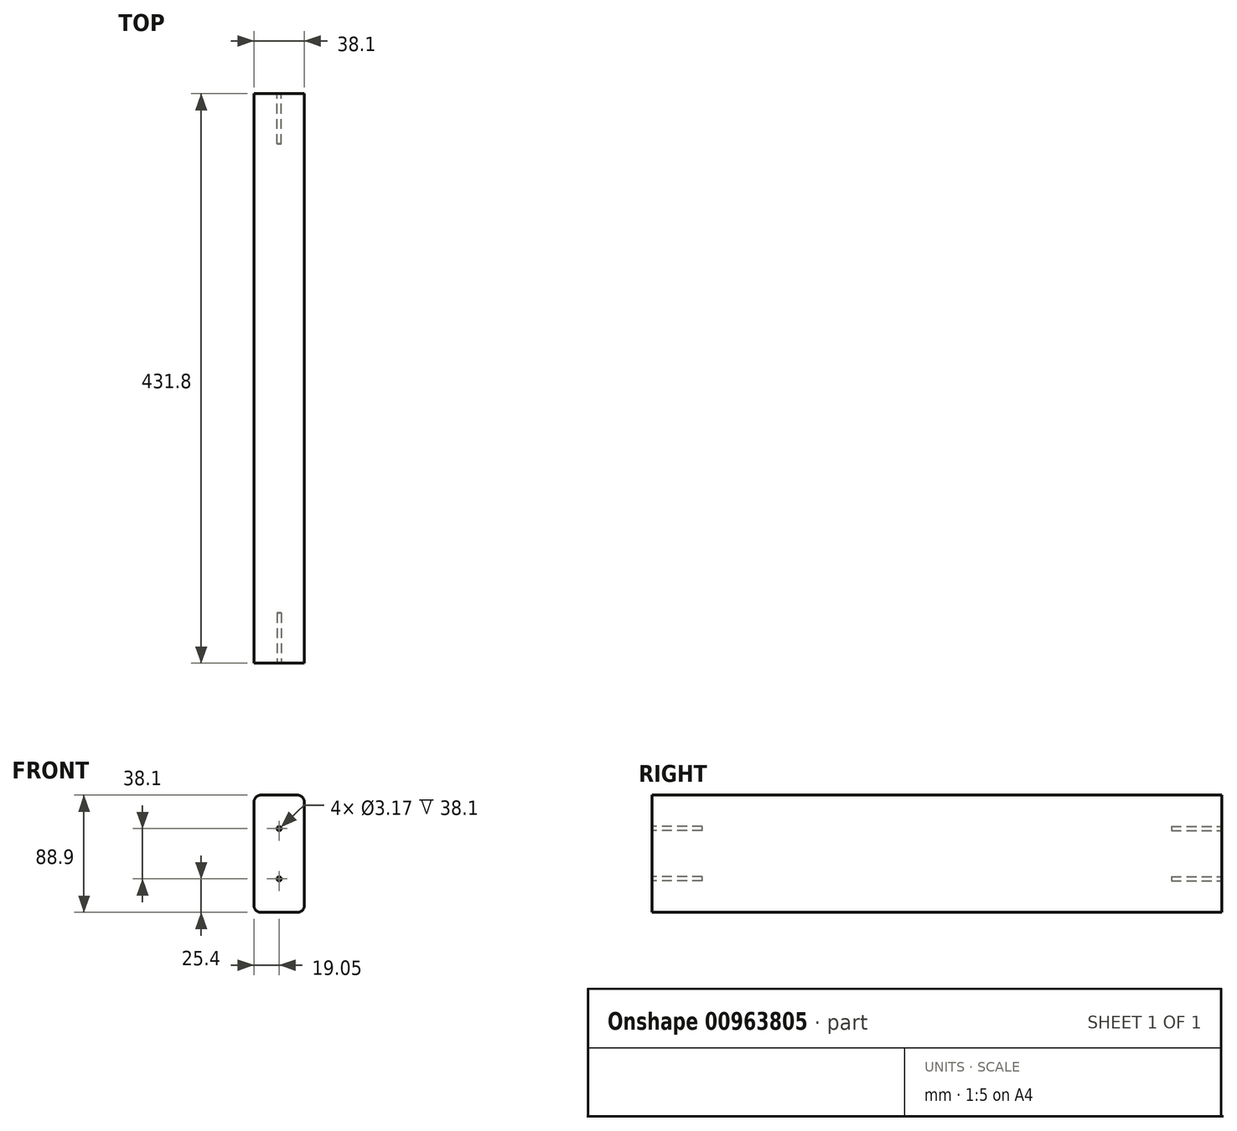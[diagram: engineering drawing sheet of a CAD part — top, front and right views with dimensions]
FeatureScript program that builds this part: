
annotation { "Feature Type Name" : "Feature", "Feature Type Description" : "" }
export const myFeature = defineFeature(function(context is Context, id is Id, definition is map)
    precondition{}
    {
        {
            var Q0;
            Q0=qCreatedBy(makeId("Front.planeOp"),FACE);
            var sketch = newSketch(context, id + "F0", { "sketchPlane" : qUnion([Q0])});
            skLineSegment(sketch, "E0.bottom", {"start": v(19.05, 44.45) * mm, "end": v(-19.05, 44.45) * mm});
            skLineSegment(sketch, "E0.top", {"start": v(19.05, -44.45) * mm, "end": v(-19.05, -44.45) * mm});
            skLineSegment(sketch, "E0.left", {"start": v(19.05, 44.45) * mm, "end": v(19.05, -44.45) * mm});
            skLineSegment(sketch, "E0.right", {"start": v(-19.05, 44.45) * mm, "end": v(-19.05, -44.45) * mm});
            skPoint(sketch, "E0.middle", {"position": v(0, 0) * mm});
            skSolve(sketch);
        }
        {
            var Q0;
            Q0=makeQuery(id+"F0.imprint","IMPRINT",FACE,{"disambiguationData":[TD([[makeQuery(id+"F0.imprint","IMPRINT",EDGE,{"derivedFrom":sQuery(id+"F0.wireOp",EDGE,"E0.bottom")}),1.0]])]});
            extrude(context, id + "F1", {"entities" : qUnion([Q0]), "endBound" : BoundingType.SYMMETRIC, "depth" : 431.8 * mm, "offsetDistance" : 25.4 * mm});
        }
        {
            var Q0;
            Q0=makeQuery(id+"F1.opExtrude","SWEPT_EDGE",EDGE,{"disambiguationData":[OSD([sQuery(id+"F0.wireOp",EDGE,"E0.bottom"),sQuery(id+"F0.wireOp",EDGE,"E0.left")])]});
            var Q1;
            Q1=makeQuery(id+"F1.opExtrude","SWEPT_EDGE",EDGE,{"disambiguationData":[OSD([sQuery(id+"F0.wireOp",EDGE,"E0.bottom"),sQuery(id+"F0.wireOp",EDGE,"E0.right")])]});
            var Q2;
            Q2=makeQuery(id+"F1.opExtrude","SWEPT_EDGE",EDGE,{"disambiguationData":[OSD([sQuery(id+"F0.wireOp",EDGE,"E0.top"),sQuery(id+"F0.wireOp",EDGE,"E0.left")])]});
            var Q3;
            Q3=makeQuery(id+"F1.opExtrude","SWEPT_EDGE",EDGE,{"disambiguationData":[OSD([sQuery(id+"F0.wireOp",EDGE,"E0.top"),sQuery(id+"F0.wireOp",EDGE,"E0.right")])]});
            fillet(context, id + "F2", {"entities" : qUnion([Q0, Q1, Q2, Q3]), "radius" : 5.08 * mm, "tangentPropagation" : true, "allowEdgeOverflow" : false});
        }
        {
            assignVariable(context, id + "F3", {"name" : "vbeam_h_drill_depth", "anyValue" : 38.1 * mm});
        }
        {
            var Q0;
            Q0=makeQuery(id+"F1.opExtrude","CAP_FACE",FACE,{"disambiguationData":[OSD([sQuery(id+"F0.wireOp",EDGE,"E0.bottom"),sQuery(id+"F0.wireOp",EDGE,"E0.top"),sQuery(id+"F0.wireOp",EDGE,"E0.left"),sQuery(id+"F0.wireOp",EDGE,"E0.right")])],"isStart":false});
            var sketch = newSketch(context, id + "F4", { "sketchPlane" : qUnion([Q0])});
            skCircle(sketch, "E1", {"center": v(0, 19.05) * mm, "radius": 1.59 * mm});
            skSolve(sketch);
        }
        {
            var Q0;
            Q0=makeQuery(id+"F4.imprint","IMPRINT",FACE,{"disambiguationData":[TD([[makeQuery(id+"F4.imprint","IMPRINT",EDGE,{"derivedFrom":sQuery(id+"F4.wireOp",EDGE,"E1")}),1.0]])]});
            extrude(context, id + "F5", {"entities" : qUnion([Q0]), "operationType" : NewBodyOperationType.REMOVE, "oppositeDirection" : true, "depth" : getVariable(context, 'vbeam_h_drill_depth'), "offsetDistance" : 25.4 * mm});
        }
        {
            var Q0;
            Q0=makeQuery(id+"F1.opExtrude","CAP_FACE",FACE,{"disambiguationData":[OSD([sQuery(id+"F0.wireOp",EDGE,"E0.bottom"),sQuery(id+"F0.wireOp",EDGE,"E0.top"),sQuery(id+"F0.wireOp",EDGE,"E0.left"),sQuery(id+"F0.wireOp",EDGE,"E0.right")])],"isStart":false});
            var sketch = newSketch(context, id + "F6", { "sketchPlane" : qUnion([Q0])});
            skCircle(sketch, "E2", {"center": v(0, -19.05) * mm, "radius": 1.59 * mm});
            skSolve(sketch);
        }
        {
            var Q0;
            Q0=makeQuery(id+"F6.imprint","IMPRINT",FACE,{"disambiguationData":[TD([[makeQuery(id+"F6.imprint","IMPRINT",EDGE,{"derivedFrom":sQuery(id+"F6.wireOp",EDGE,"E2")}),1.0]])]});
            extrude(context, id + "F7", {"entities" : qUnion([Q0]), "operationType" : NewBodyOperationType.REMOVE, "oppositeDirection" : true, "depth" : getVariable(context, 'vbeam_h_drill_depth'), "offsetDistance" : 25.4 * mm});
        }
        {
            var Q0;
            Q0=makeQuery(id+"F1.opExtrude","CAP_FACE",FACE,{"disambiguationData":[OSD([sQuery(id+"F0.wireOp",EDGE,"E0.bottom"),sQuery(id+"F0.wireOp",EDGE,"E0.top"),sQuery(id+"F0.wireOp",EDGE,"E0.left"),sQuery(id+"F0.wireOp",EDGE,"E0.right")])],"isStart":true});
            var sketch = newSketch(context, id + "F8", { "sketchPlane" : qUnion([Q0])});
            skCircle(sketch, "E3", {"center": v(0, 19.05) * mm, "radius": 1.59 * mm});
            skSolve(sketch);
        }
        {
            var Q0;
            Q0=makeQuery(id+"F8.imprint","IMPRINT",FACE,{"disambiguationData":[TD([[makeQuery(id+"F8.imprint","IMPRINT",EDGE,{"derivedFrom":sQuery(id+"F8.wireOp",EDGE,"E3")}),1.0]])]});
            extrude(context, id + "F9", {"entities" : qUnion([Q0]), "operationType" : NewBodyOperationType.REMOVE, "oppositeDirection" : true, "depth" : getVariable(context, 'vbeam_h_drill_depth'), "offsetDistance" : 25.4 * mm});
        }
        {
            var Q0;
            Q0=makeQuery(id+"F1.opExtrude","CAP_FACE",FACE,{"disambiguationData":[OSD([sQuery(id+"F0.wireOp",EDGE,"E0.bottom"),sQuery(id+"F0.wireOp",EDGE,"E0.top"),sQuery(id+"F0.wireOp",EDGE,"E0.left"),sQuery(id+"F0.wireOp",EDGE,"E0.right")])],"isStart":true});
            var sketch = newSketch(context, id + "F10", { "sketchPlane" : qUnion([Q0])});
            skCircle(sketch, "E4", {"center": v(0, -19.05) * mm, "radius": 1.59 * mm});
            skSolve(sketch);
        }
        {
            var Q0;
            Q0=makeQuery(id+"F10.imprint","IMPRINT",FACE,{"disambiguationData":[TD([[makeQuery(id+"F10.imprint","IMPRINT",EDGE,{"derivedFrom":sQuery(id+"F10.wireOp",EDGE,"E4")}),1.0]])]});
            extrude(context, id + "F11", {"entities" : qUnion([Q0]), "operationType" : NewBodyOperationType.REMOVE, "oppositeDirection" : true, "depth" : getVariable(context, 'vbeam_h_drill_depth'), "offsetDistance" : 25.4 * mm});
        }
    });
